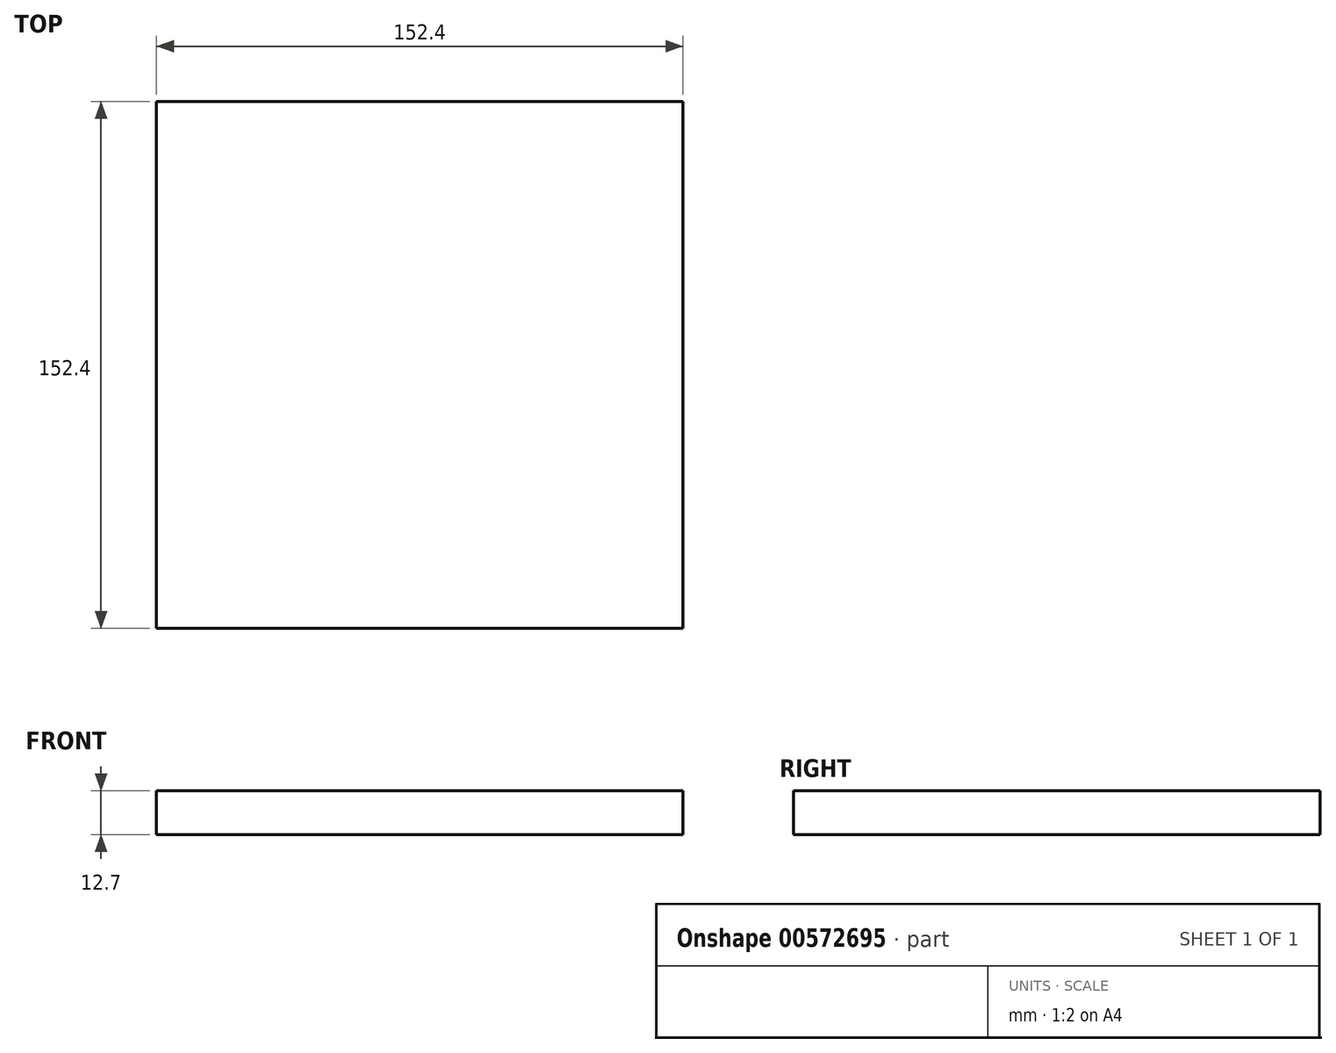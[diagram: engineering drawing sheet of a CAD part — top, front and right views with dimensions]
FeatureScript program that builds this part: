
annotation { "Feature Type Name" : "Feature", "Feature Type Description" : "" }
export const myFeature = defineFeature(function(context is Context, id is Id, definition is map)
    precondition{}
    {
        {
            var Q0;
            Q0=qCreatedBy(makeId("Top.planeOp"),FACE);
            var sketch = newSketch(context, id + "F0", { "sketchPlane" : qUnion([Q0])});
            skLineSegment(sketch, "E0.bottom", {"start": v(0, 0) * mm, "end": v(152.4, 0) * mm});
            skLineSegment(sketch, "E0.top", {"start": v(0, 152.4) * mm, "end": v(152.4, 152.4) * mm});
            skLineSegment(sketch, "E0.left", {"start": v(0, 0) * mm, "end": v(0, 152.4) * mm});
            skLineSegment(sketch, "E0.right", {"start": v(152.4, 0) * mm, "end": v(152.4, 152.4) * mm});
            skLineSegment(sketch, "E1", {"start": v(76.2, 152.4) * mm, "end": v(76.2, 0) * mm, "construction": true});
            skLineSegment(sketch, "E2", {"start": v(152.4, 76.2) * mm, "end": v(0, 76.2) * mm, "construction": true});
            skLineSegment(sketch, "E3", {"start": v(101.6, 0) * mm, "end": v(101.6, 152.4) * mm, "construction": true});
            skLineSegment(sketch, "E4", {"start": v(50.8, 0) * mm, "end": v(50.8, 152.4) * mm, "construction": true});
            skSolve(sketch);
        }
        {
            var Q0;
            Q0 = qSketchRegion(id + "F0", true);
            extrude(context, id + "F1", {"entities" : qUnion([Q0]), "depth" : 12.7 * mm, "offsetDistance" : 25.4 * mm});
        }
    });
